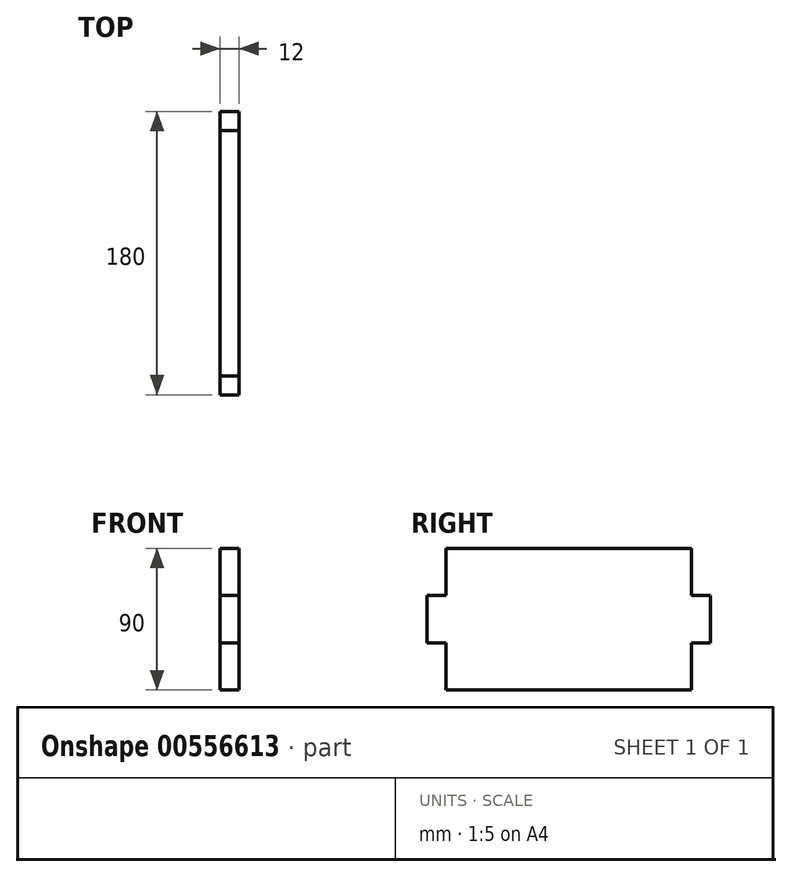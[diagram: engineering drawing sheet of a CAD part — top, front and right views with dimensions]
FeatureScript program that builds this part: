
annotation { "Feature Type Name" : "Feature", "Feature Type Description" : "" }
export const myFeature = defineFeature(function(context is Context, id is Id, definition is map)
    precondition{}
    {
        {
            var Q0;
            Q0=qCreatedBy(makeId("Right.planeOp"),FACE);
            var sketch = newSketch(context, id + "F0", { "sketchPlane" : qUnion([Q0])});
            skLineSegment(sketch, "E0", {"start": v(0, 0) * mm, "end": v(0, 30) * mm});
            skLineSegment(sketch, "E1", {"start": v(0, 30) * mm, "end": v(-12, 30) * mm});
            skLineSegment(sketch, "E2", {"start": v(-12, 30) * mm, "end": v(-12, 60) * mm});
            skLineSegment(sketch, "E3", {"start": v(-12, 60) * mm, "end": v(0, 60) * mm});
            skLineSegment(sketch, "E4", {"start": v(0, 60) * mm, "end": v(0, 90) * mm});
            skLineSegment(sketch, "E5", {"start": v(0, 90) * mm, "end": v(78, 90) * mm});
            skLineSegment(sketch, "E6", {"start": v(78, 90) * mm, "end": v(78, 0) * mm, "construction": true});
            skLineSegment(sketch, "E7", {"start": v(78, 0) * mm, "end": v(0, 0) * mm});
            skLineSegment(sketch, "E8.MirrorCS", {"start": v(168, 60) * mm, "end": v(156, 60) * mm});
            skLineSegment(sketch, "E9.MirrorCS", {"start": v(78, 0) * mm, "end": v(156, 0) * mm});
            skLineSegment(sketch, "E10.MirrorCS", {"start": v(156, 60) * mm, "end": v(156, 90) * mm});
            skLineSegment(sketch, "E11.MirrorCS", {"start": v(156, 30) * mm, "end": v(168, 30) * mm});
            skLineSegment(sketch, "E12.MirrorCS", {"start": v(168, 30) * mm, "end": v(168, 60) * mm});
            skLineSegment(sketch, "E13.MirrorCS", {"start": v(156, 0) * mm, "end": v(156, 30) * mm});
            skLineSegment(sketch, "E14.MirrorCS", {"start": v(156, 90) * mm, "end": v(78, 90) * mm});
            skSolve(sketch);
        }
        {
            var Q0;
            Q0 = qSketchRegion(id + "F0", true);
            extrude(context, id + "F1", {"entities" : qUnion([Q0]), "endBound" : BoundingType.SYMMETRIC, "depth" : 12 * mm, "offsetDistance" : 25 * mm});
        }
    });
